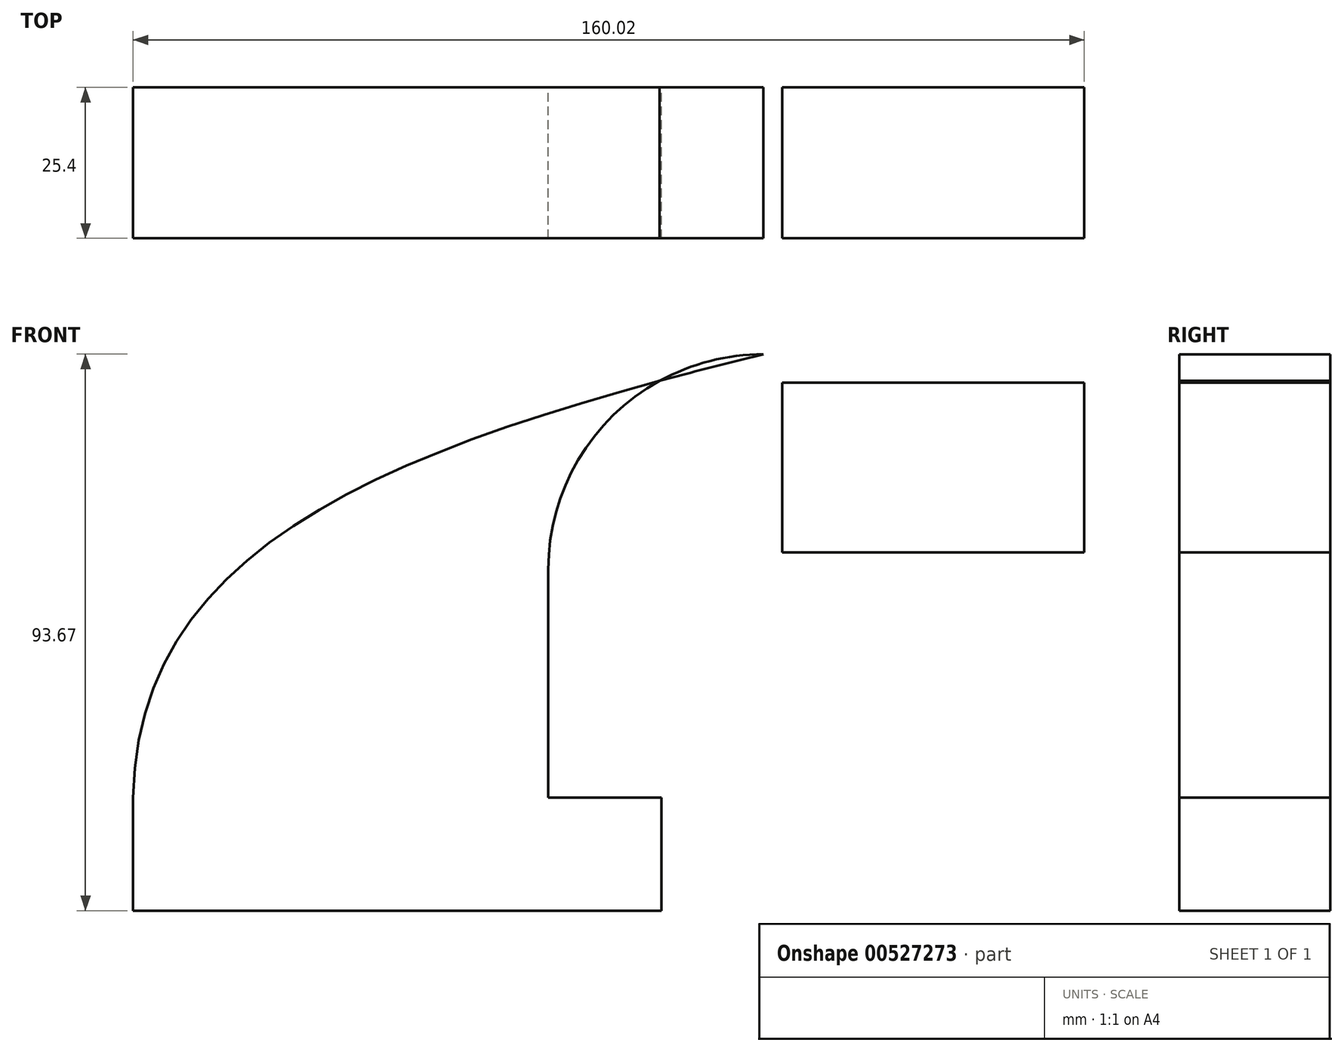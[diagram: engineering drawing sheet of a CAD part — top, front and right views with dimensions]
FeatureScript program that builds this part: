
annotation { "Feature Type Name" : "Feature", "Feature Type Description" : "" }
export const myFeature = defineFeature(function(context is Context, id is Id, definition is map)
    precondition{}
    {
        {
            var Q0;
            Q0=qCreatedBy(makeId("Front.planeOp"),FACE);
            var sketch = newSketch(context, id + "F0", { "sketchPlane" : qUnion([Q0])});
            skLineSegment(sketch, "E0.bottom", {"start": v(-44.45, -9.52) * mm, "end": v(44.45, -9.52) * mm});
            skLineSegment(sketch, "E0.top", {"start": v(-44.45, 9.52) * mm, "end": v(44.45, 9.52) * mm});
            skLineSegment(sketch, "E0.left", {"start": v(-44.45, -9.52) * mm, "end": v(-44.45, 9.52) * mm});
            skLineSegment(sketch, "E0.right", {"start": v(44.45, -9.52) * mm, "end": v(44.45, 9.52) * mm});
            skPoint(sketch, "E0.middle", {"position": v(0, 0) * mm});
            skLineSegment(sketch, "E1.bottom", {"start": v(115.57, 50.8) * mm, "end": v(64.77, 50.8) * mm});
            skLineSegment(sketch, "E1.top", {"start": v(115.57, 79.38) * mm, "end": v(64.77, 79.38) * mm});
            skLineSegment(sketch, "E1.left", {"start": v(115.57, 50.8) * mm, "end": v(115.57, 79.38) * mm});
            skLineSegment(sketch, "E1.right", {"start": v(64.77, 50.8) * mm, "end": v(64.77, 79.38) * mm});
            skPoint(sketch, "E1.middle", {"position": v(90.17, 65.09) * mm});
            skLineSegment(sketch, "E2", {"start": v(44.45, 9.52) * mm, "end": v(44.45, 47.94) * mm});
            skPoint(sketch, "E3.endSnap0", {"position": v(90.17, 50.8) * mm});
            skArc(sketch, "E4", {"start": v(44.45, 47.94) * mm, "mid": v(49.47, 60.07) * mm, "end": v(61.6, 65.09) * mm});
            skPoint(sketch, "E4.endSnap0", {"position": v(64.77, 65.09) * mm});
            skLineSegment(sketch, "E5", {"start": v(61.6, 65.09) * mm, "end": v(100.28, 65.09) * mm});
            skLineSegment(sketch, "E6.0", {"start": v(61.6, 84.14) * mm, "end": v(100.28, 84.14) * mm});
            skArc(sketch, "E6.1", {"start": v(25.4, 47.94) * mm, "mid": v(36, 73.54) * mm, "end": v(61.6, 84.14) * mm});
            skLineSegment(sketch, "E6.2", {"start": v(25.4, 9.52) * mm, "end": v(25.4, 47.94) * mm});
            skFitSpline(sketch, "E7", {"points": [v(61.6, 84.14) * mm, v(-44.45, 9.52) * mm], "startDerivative": vector(-184.79, -45.54) * mm, "endDerivative": vector(-2.02, -129.01) * mm});
            skSolve(sketch);
        }
        {
            var Q0;
            Q0 = qSketchRegion(id + "F0", true);
            extrude(context, id + "F1", {"entities" : qUnion([Q0]), "depth" : 25.4 * mm, "offsetDistance" : 25.4 * mm});
        }
    });
